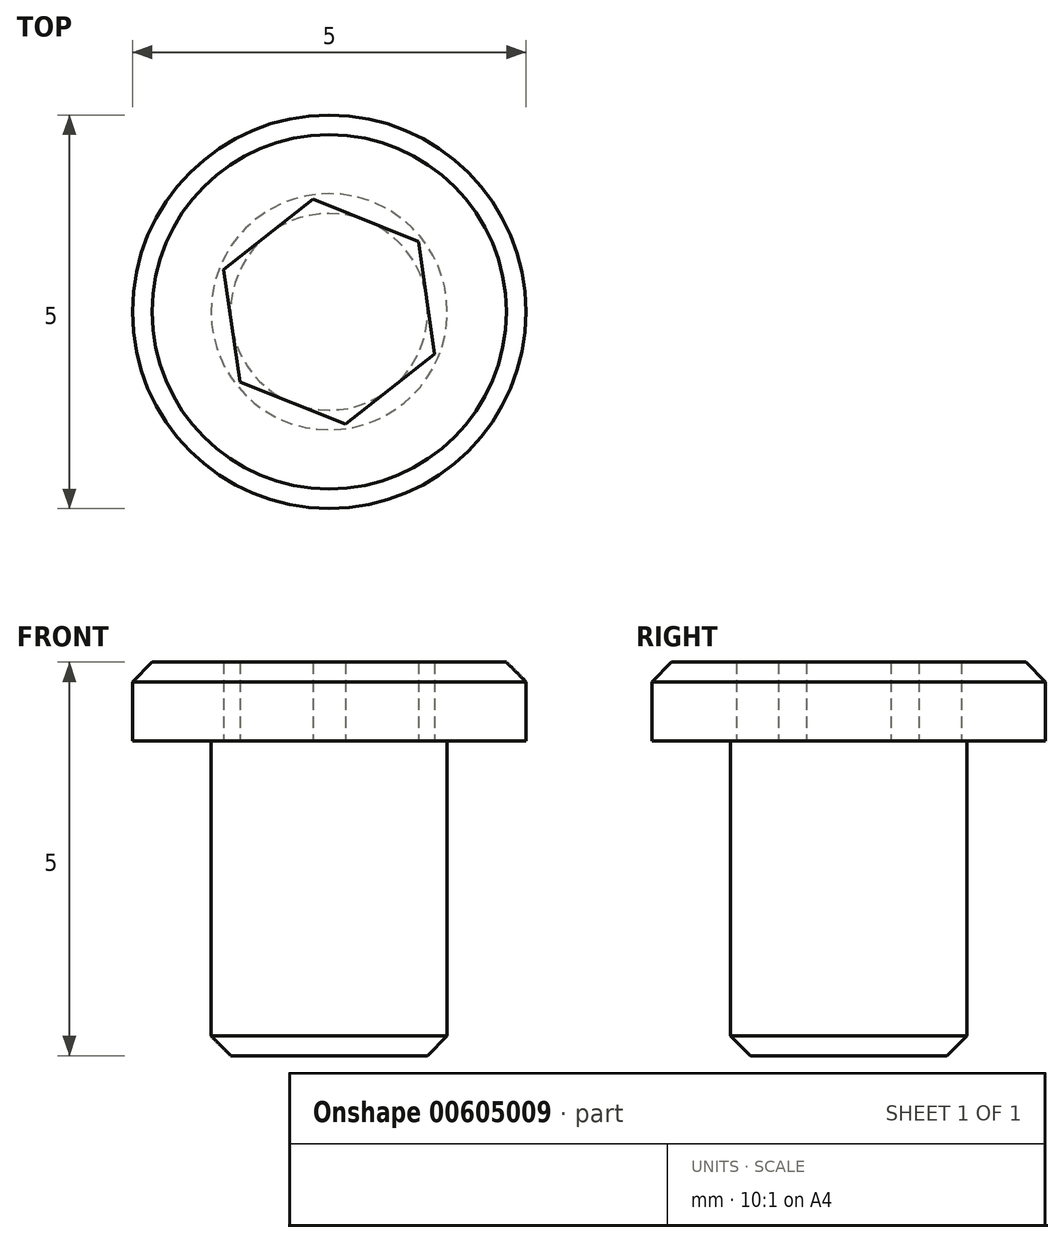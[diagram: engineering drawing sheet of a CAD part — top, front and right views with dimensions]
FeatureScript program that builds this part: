
annotation { "Feature Type Name" : "Feature", "Feature Type Description" : "" }
export const myFeature = defineFeature(function(context is Context, id is Id, definition is map)
    precondition{}
    {
        {
            var Q0;
            Q0=qCreatedBy(makeId("Top.planeOp"),FACE);
            var sketch = newSketch(context, id + "F0", { "sketchPlane" : qUnion([Q0])});
            skCircle(sketch, "E0", {"center": v(0, 0) * mm, "radius": 2.5 * mm});
            skCircle(sketch, "E1.cCircle", {"center": v(0, 0) * mm, "radius": 1.25 * mm, "construction": true});
            skLineSegment(sketch, "E1.0", {"start": v(1.34, -0.54) * mm, "end": v(0.2, -1.43) * mm});
            skLineSegment(sketch, "E1.1", {"start": v(0.2, -1.43) * mm, "end": v(-1.13, -0.9) * mm});
            skLineSegment(sketch, "E1.2", {"start": v(-1.13, -0.9) * mm, "end": v(-1.34, 0.54) * mm});
            skLineSegment(sketch, "E1.3", {"start": v(-1.34, 0.54) * mm, "end": v(-0.2, 1.43) * mm});
            skLineSegment(sketch, "E1.4", {"start": v(-0.2, 1.43) * mm, "end": v(1.13, 0.9) * mm});
            skLineSegment(sketch, "E1.5", {"start": v(1.13, 0.9) * mm, "end": v(1.34, -0.54) * mm});
            skPoint(sketch, "E1.0.midPoint", {"position": v(0.77, -0.98) * mm});
            skSolve(sketch);
        }
        {
            var Q0;
            Q0 = qSketchRegion(id + "F0", true);
            extrude(context, id + "F1", {"entities" : qUnion([Q0]), "depth" : 1 * mm, "offsetDistance" : 25 * mm});
        }
        {
            var Q0;
            Q0=makeQuery(id+"F1.opExtrude","CAP_FACE",FACE,{"disambiguationData":[OSD([sQuery(id+"F0.wireOp",EDGE,"E0"),sQuery(id+"F0.wireOp",EDGE,"E1.0"),sQuery(id+"F0.wireOp",EDGE,"E1.1"),sQuery(id+"F0.wireOp",EDGE,"E1.2"),sQuery(id+"F0.wireOp",EDGE,"E1.3"),sQuery(id+"F0.wireOp",EDGE,"E1.4"),sQuery(id+"F0.wireOp",EDGE,"E1.5")])],"isStart":true});
            var sketch = newSketch(context, id + "F2", { "sketchPlane" : qUnion([Q0])});
            skCircle(sketch, "E2", {"center": v(0, 0) * mm, "radius": 1.5 * mm});
            skSolve(sketch);
        }
        {
            var Q0;
            Q0 = qSketchRegion(id + "F2", true);
            extrude(context, id + "F3", {"entities" : qUnion([Q0]), "operationType" : NewBodyOperationType.ADD, "depth" : 4 * mm, "offsetDistance" : 25 * mm});
        }
        {
            var Q0;
            Q0=makeQuery(id+"F1.opExtrude","CAP_EDGE",EDGE,{"disambiguationData":[OSD([sQuery(id+"F0.wireOp",EDGE,"E0")])],"isStart":false});
            chamfer(context, id + "F4", {"entities" : qUnion([Q0]), "width" : 0.25 * mm, "tangentPropagation" : true});
        }
        {
            var Q0;
            Q0=makeQuery(id+"F3.opExtrude","CAP_FACE",FACE,{"disambiguationData":[OSD([sQuery(id+"F2.wireOp",EDGE,"E2")])],"isStart":false});
            chamfer(context, id + "F5", {"entities" : qUnion([Q0]), "width" : 0.25 * mm, "tangentPropagation" : true});
        }
    });
